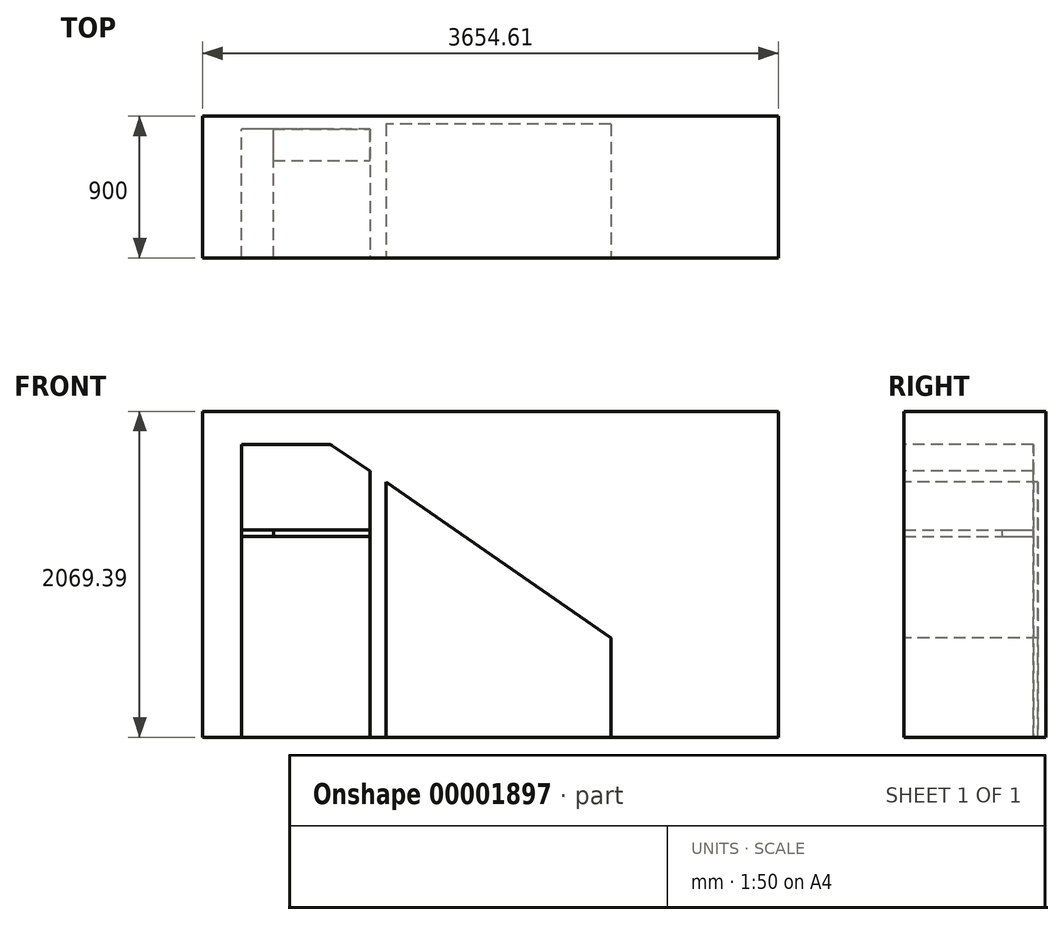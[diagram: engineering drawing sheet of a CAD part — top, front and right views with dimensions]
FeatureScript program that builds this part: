
annotation { "Feature Type Name" : "Feature", "Feature Type Description" : "" }
export const myFeature = defineFeature(function(context is Context, id is Id, definition is map)
    precondition{}
    {
        {
            var Q0;
            Q0=qCreatedBy(makeId("Front.planeOp"),FACE);
            var sketch = newSketch(context, id + "F0", { "sketchPlane" : qUnion([Q0])});
            skLineSegment(sketch, "E0", {"start": v(-1010.68, -1409.3) * mm, "end": v(-195.68, -1409.3) * mm});
            skLineSegment(sketch, "E1", {"start": v(-195.68, -1409.3) * mm, "end": v(-195.68, 280.7) * mm});
            skLineSegment(sketch, "E2", {"start": v(-195.68, 280.7) * mm, "end": v(-432.96, 442.05) * mm});
            skLineSegment(sketch, "E3", {"start": v(-461.07, 450.7) * mm, "end": v(-1010.68, 450.7) * mm});
            skLineSegment(sketch, "E4", {"start": v(-1010.68, 450.7) * mm, "end": v(-1010.68, -1409.3) * mm});
            skLineSegment(sketch, "E5", {"start": v(-95.68, 210.7) * mm, "end": v(-95.68, -1409.3) * mm});
            skLineSegment(sketch, "E6", {"start": v(-95.68, -1409.3) * mm, "end": v(1334.32, -1409.3) * mm});
            skLineSegment(sketch, "E7", {"start": v(1334.32, -1409.3) * mm, "end": v(1334.32, -779.3) * mm});
            skLineSegment(sketch, "E8", {"start": v(1334.32, -779.3) * mm, "end": v(-95.68, 210.7) * mm});
            skPoint(sketch, "E9.visualSharp", {"position": v(-445.68, 450.7) * mm});
            skArc(sketch, "E9.filletArc", {"start": v(-432.96, 442.05) * mm, "mid": v(-446.37, 448.49) * mm, "end": v(-461.07, 450.7) * mm});
            skLineSegment(sketch, "E10.bottom", {"start": v(-1258.48, -1409.3) * mm, "end": v(2396.13, -1409.3) * mm});
            skLineSegment(sketch, "E10.top", {"start": v(-1258.48, 660.1) * mm, "end": v(2396.13, 660.1) * mm});
            skLineSegment(sketch, "E10.left", {"start": v(-1258.48, -1409.3) * mm, "end": v(-1258.48, 660.1) * mm});
            skLineSegment(sketch, "E10.right", {"start": v(2396.13, -1409.3) * mm, "end": v(2396.13, 660.1) * mm});
            skSolve(sketch);
        }
        {
            var Q0;
            {var subQ3=sQuery(id+"F0.wireOp",EDGE,"E1");Q0=makeQuery(id+"F0.imprint","IMPRINT",FACE,{"disambiguationData":[TD([[makeQuery(id+"F0.imprint","IMPRINT",EDGE,{"derivedFrom":subQ3}),-1.0]])]});}
            extrude(context, id + "F1", {"entities" : qUnion([Q0]), "oppositeDirection" : true, "depth" : 900 * mm});
        }
        {
            var Q0;
            Q0=makeQuery(id+"F1.opExtrude","CAP_FACE",FACE,{"disambiguationData":[OSD([sQuery(id+"F0.wireOp",EDGE,"E1"),sQuery(id+"F0.wireOp",EDGE,"E2"),sQuery(id+"F0.wireOp",EDGE,"E3"),sQuery(id+"F0.wireOp",EDGE,"E4"),sQuery(id+"F0.wireOp",EDGE,"E5"),sQuery(id+"F0.wireOp",EDGE,"E7"),sQuery(id+"F0.wireOp",EDGE,"E8"),sQuery(id+"F0.wireOp",EDGE,"E9.filletArc"),sQuery(id+"F0.wireOp",EDGE,"E10.bottom"),sQuery(id+"F0.wireOp",EDGE,"E10.top"),sQuery(id+"F0.wireOp",EDGE,"E10.left"),sQuery(id+"F0.wireOp",EDGE,"E10.right")])],"isStart":false});
            var sketch = newSketch(context, id + "F2", { "sketchPlane" : qUnion([Q0])});
            skLineSegment(sketch, "E11", {"start": v(-1334.32, -1409.3) * mm, "end": v(95.68, -1409.3) * mm});
            skLineSegment(sketch, "E12", {"start": v(195.68, -1409.3) * mm, "end": v(1010.68, -1409.3) * mm});
            skSolve(sketch);
        }
        {
            var Q0;
            Q0=makeQuery(id+"F2.imprint","IMPRINT",FACE,{"disambiguationData":[TD([[makeQuery(id+"F2.imprint","IMPRINT",EDGE,{"derivedFrom":sQuery(id+"F2.wireOp",EDGE,"E12")}),1.0]])]});
            extrude(context, id + "F3", {"entities" : qUnion([Q0]), "operationType" : NewBodyOperationType.ADD, "oppositeDirection" : true, "depth" : 80 * mm});
        }
        {
            var Q0;
            {var subQ0=sQuery(id+"F0.wireOp",EDGE,"E1");var subQ1=sQuery(id+"F0.wireOp",EDGE,"E2");var subQ2=sQuery(id+"F0.wireOp",EDGE,"E3");var subQ3=sQuery(id+"F0.wireOp",EDGE,"E4");var subQ4=sQuery(id+"F0.wireOp",EDGE,"E9.filletArc");Q0=makeQuery(id+"F3.boolean.opBoolean","MERGE",FACE,{"derivedFrom":[makeQuery(id+"F1.opExtrude","CAP_FACE",FACE,{"disambiguationData":[OSD([subQ0,subQ1,subQ2,subQ3,sQuery(id+"F0.wireOp",EDGE,"E5"),sQuery(id+"F0.wireOp",EDGE,"E7"),sQuery(id+"F0.wireOp",EDGE,"E8"),subQ4,sQuery(id+"F0.wireOp",EDGE,"E10.bottom"),sQuery(id+"F0.wireOp",EDGE,"E10.top"),sQuery(id+"F0.wireOp",EDGE,"E10.left"),sQuery(id+"F0.wireOp",EDGE,"E10.right")])],"isStart":false}),makeQuery(id+"F3.opExtrude","CAP_FACE",FACE,{"disambiguationData":[OSD([subQ0,subQ1,subQ2,subQ3,subQ4,sQuery(id+"F2.wireOp",EDGE,"E12")])],"isStart":true})]});}
            var sketch = newSketch(context, id + "F4", { "sketchPlane" : qUnion([Q0])});
            skLineSegment(sketch, "E13", {"start": v(-1334.32, -1409.3) * mm, "end": v(95.68, -1409.3) * mm});
            skSolve(sketch);
        }
        {
            var Q0;
            Q0=makeQuery(id+"F4.imprint","IMPRINT",FACE,{"disambiguationData":[TD([[makeQuery(id+"F4.imprint","IMPRINT",EDGE,{"derivedFrom":sQuery(id+"F4.wireOp",EDGE,"E13")}),1.0]])]});
            extrude(context, id + "F5", {"entities" : qUnion([Q0]), "operationType" : NewBodyOperationType.ADD, "oppositeDirection" : true, "depth" : 50 * mm});
        }
        {
            var Q0;
            Q0=makeQuery(id+"F1.opExtrude","SWEPT_FACE",FACE,{"disambiguationData":[OSD([sQuery(id+"F0.wireOp",EDGE,"E4")])]});
            var sketch = newSketch(context, id + "F6", { "sketchPlane" : qUnion([Q0])});
            skLineSegment(sketch, "E14.bottom", {"start": v(0, -93.76) * mm, "end": v(820, -93.76) * mm});
            skLineSegment(sketch, "E14.top", {"start": v(0, -133.76) * mm, "end": v(820, -133.76) * mm});
            skLineSegment(sketch, "E14.left", {"start": v(0, -93.76) * mm, "end": v(0, -133.76) * mm});
            skLineSegment(sketch, "E14.right", {"start": v(820, -93.76) * mm, "end": v(820, -133.76) * mm});
            skSolve(sketch);
        }
        {
            var Q0;
            Q0=makeQuery(id+"F6.imprint","IMPRINT",FACE,{"disambiguationData":[TD([[makeQuery(id+"F6.imprint","IMPRINT",EDGE,{"derivedFrom":sQuery(id+"F6.wireOp",EDGE,"E14.bottom")}),-1.0]])]});
            extrude(context, id + "F7", {"entities" : qUnion([Q0]), "depth" : 200 * mm});
        }
        {
            var Q0;
            Q0=makeQuery(id+"F3.opExtrude","CAP_FACE",FACE,{"disambiguationData":[OSD([sQuery(id+"F0.wireOp",EDGE,"E1"),sQuery(id+"F0.wireOp",EDGE,"E2"),sQuery(id+"F0.wireOp",EDGE,"E3"),sQuery(id+"F0.wireOp",EDGE,"E4"),sQuery(id+"F0.wireOp",EDGE,"E9.filletArc"),sQuery(id+"F2.wireOp",EDGE,"E12")])],"isStart":false});
            var sketch = newSketch(context, id + "F8", { "sketchPlane" : qUnion([Q0])});
            skLineSegment(sketch, "E15.bottom", {"start": v(-810.68, -93.76) * mm, "end": v(-195.68, -93.76) * mm});
            skLineSegment(sketch, "E15.top", {"start": v(-810.68, -133.76) * mm, "end": v(-195.68, -133.76) * mm});
            skLineSegment(sketch, "E15.left", {"start": v(-810.68, -93.76) * mm, "end": v(-810.68, -133.76) * mm});
            skLineSegment(sketch, "E15.right", {"start": v(-195.68, -93.76) * mm, "end": v(-195.68, -133.76) * mm});
            skSolve(sketch);
        }
        {
            var Q0;
            Q0=makeQuery(id+"F8.imprint","IMPRINT",FACE,{"disambiguationData":[TD([[makeQuery(id+"F8.imprint","IMPRINT",EDGE,{"derivedFrom":sQuery(id+"F8.wireOp",EDGE,"E15.bottom")}),-1.0]])]});
            extrude(context, id + "F9", {"entities" : qUnion([Q0]), "depth" : 200 * mm});
        }
    });
